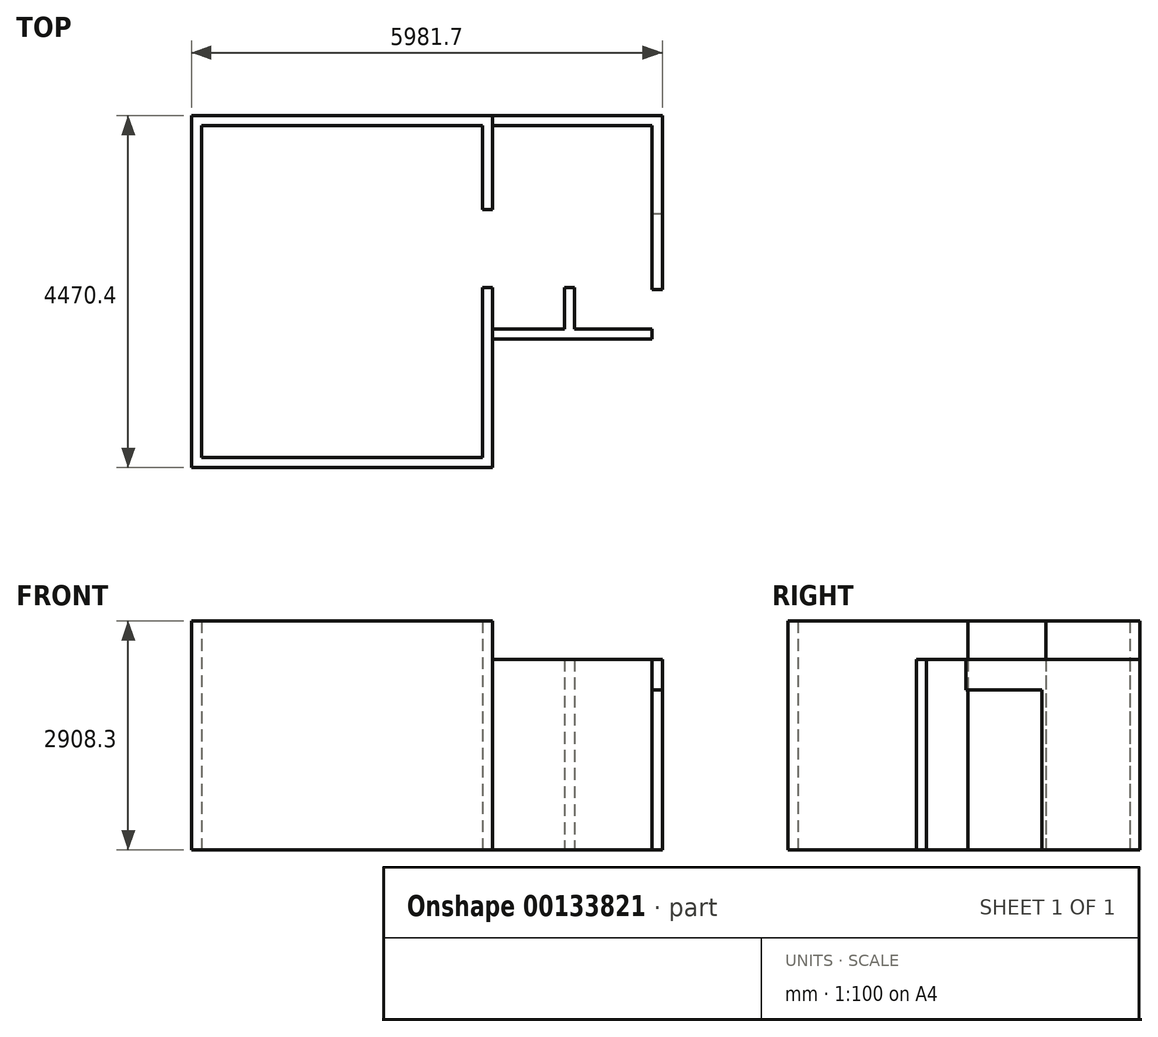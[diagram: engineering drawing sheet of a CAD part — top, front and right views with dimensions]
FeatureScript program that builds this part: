
annotation { "Feature Type Name" : "Feature", "Feature Type Description" : "" }
export const myFeature = defineFeature(function(context is Context, id is Id, definition is map)
    precondition{}
    {
        {
            var Q0;
            Q0=qCreatedBy(makeId("Top.planeOp"),FACE);
            var sketch = newSketch(context, id + "F0", { "sketchPlane" : qUnion([Q0])});
            skLineSegment(sketch, "E0.bottom", {"start": v(-3695.7, 2908.4) * mm, "end": v(-127, 2908.4) * mm});
            skLineSegment(sketch, "E0.top", {"start": v(-3695.7, -1308) * mm, "end": v(-127, -1308) * mm});
            skLineSegment(sketch, "E0.left", {"start": v(-3695.7, 2908.4) * mm, "end": v(-3695.7, -1308) * mm});
            skLineSegment(sketch, "E0.right", {"start": v(-127, 2908.4) * mm, "end": v(-127, -1308) * mm});
            skLineSegment(sketch, "E1.bottom", {"start": v(-3695.7, 2908.4) * mm, "end": v(-3479.8, 2908.4) * mm});
            skLineSegment(sketch, "E1.top", {"start": v(-3695.7, 2711.54) * mm, "end": v(-3479.8, 2711.54) * mm});
            skLineSegment(sketch, "E1.left", {"start": v(-3695.7, 2908.4) * mm, "end": v(-3695.7, 2711.54) * mm});
            skLineSegment(sketch, "E1.right", {"start": v(-3479.8, 2908.4) * mm, "end": v(-3479.8, 2711.54) * mm});
            skLineSegment(sketch, "E2.bottom", {"start": v(-127, 2908.4) * mm, "end": v(0, 2908.4) * mm});
            skLineSegment(sketch, "E2.top", {"start": v(-127, 1841.6) * mm, "end": v(0, 1841.6) * mm});
            skLineSegment(sketch, "E2.left", {"start": v(-127, 2908.4) * mm, "end": v(-127, 1841.6) * mm});
            skLineSegment(sketch, "E2.right", {"start": v(0, 2908.4) * mm, "end": v(0, 1841.6) * mm});
            skLineSegment(sketch, "E3.bottom", {"start": v(-127, -1308) * mm, "end": v(0, -1308) * mm});
            skLineSegment(sketch, "E3.top", {"start": v(-127, 851) * mm, "end": v(0, 851) * mm});
            skLineSegment(sketch, "E3.left", {"start": v(-127, -1308) * mm, "end": v(-127, 851) * mm});
            skLineSegment(sketch, "E3.right", {"start": v(0, -1308) * mm, "end": v(0, 851) * mm});
            skLineSegment(sketch, "E4.bottom", {"start": v(-3695.7, -1308) * mm, "end": v(-3479.8, -1308) * mm});
            skLineSegment(sketch, "E4.top", {"start": v(-3695.7, -1136.56) * mm, "end": v(-3479.8, -1136.56) * mm});
            skLineSegment(sketch, "E4.left", {"start": v(-3695.7, -1308) * mm, "end": v(-3695.7, -1136.56) * mm});
            skLineSegment(sketch, "E4.right", {"start": v(-3479.8, -1308) * mm, "end": v(-3479.8, -1136.56) * mm});
            skLineSegment(sketch, "E5.bottom", {"start": v(0, 851) * mm, "end": v(914.4, 851) * mm});
            skLineSegment(sketch, "E5.top", {"start": v(0, 323.94) * mm, "end": v(914.4, 323.94) * mm});
            skLineSegment(sketch, "E5.left", {"start": v(0, 851) * mm, "end": v(0, 323.94) * mm});
            skLineSegment(sketch, "E5.right", {"start": v(914.4, 851) * mm, "end": v(914.4, 323.94) * mm});
            skLineSegment(sketch, "E6.bottom", {"start": v(0, -1308) * mm, "end": v(2032, -1308) * mm});
            skLineSegment(sketch, "E6.top", {"start": v(0, 2908.4) * mm, "end": v(2032, 2908.4) * mm});
            skLineSegment(sketch, "E6.left", {"start": v(0, -1308) * mm, "end": v(0, 2908.4) * mm});
            skLineSegment(sketch, "E6.right", {"start": v(2032, -1308) * mm, "end": v(2032, 2908.4) * mm});
            skLineSegment(sketch, "E7.bottom", {"start": v(2032, 1790.8) * mm, "end": v(2184.4, 1790.8) * mm});
            skLineSegment(sketch, "E7.top", {"start": v(2032, 825.6) * mm, "end": v(2184.4, 825.6) * mm});
            skLineSegment(sketch, "E7.left", {"start": v(2032, 1790.8) * mm, "end": v(2032, 825.6) * mm});
            skLineSegment(sketch, "E7.right", {"start": v(2184.4, 1790.8) * mm, "end": v(2184.4, 825.6) * mm});
            skLineSegment(sketch, "E8.bottom", {"start": v(0, 323.94) * mm, "end": v(2032, 323.94) * mm});
            skLineSegment(sketch, "E8.left", {"start": v(0, 323.94) * mm, "end": v(0, -1308) * mm});
            skLineSegment(sketch, "E8.right", {"start": v(2032, 323.94) * mm, "end": v(2032, -1308) * mm});
            skLineSegment(sketch, "E9.bottom", {"start": v(2159, -1435) * mm, "end": v(-3822.7, -1435) * mm});
            skLineSegment(sketch, "E9.top", {"start": v(2159, 3035.4) * mm, "end": v(-3822.7, 3035.4) * mm});
            skLineSegment(sketch, "E9.left", {"start": v(2159, -1435) * mm, "end": v(2159, 3035.4) * mm});
            skLineSegment(sketch, "E9.right", {"start": v(-3822.7, -1435) * mm, "end": v(-3822.7, 3035.4) * mm});
            skLineSegment(sketch, "E10", {"start": v(0, -1308) * mm, "end": v(0, -1435) * mm});
            skLineSegment(sketch, "E11", {"start": v(0, 2908.4) * mm, "end": v(0, 3035.4) * mm});
            skLineSegment(sketch, "E12.bottom", {"start": v(914.4, 851) * mm, "end": v(1041.4, 851) * mm});
            skLineSegment(sketch, "E12.top", {"start": v(914.4, 323.94) * mm, "end": v(1041.4, 323.94) * mm});
            skLineSegment(sketch, "E12.right", {"start": v(1041.4, 851) * mm, "end": v(1041.4, 323.94) * mm});
            skLineSegment(sketch, "E13.top", {"start": v(0, 196.94) * mm, "end": v(2032, 196.94) * mm});
            skLineSegment(sketch, "E13.left", {"start": v(0, 323.94) * mm, "end": v(0, 196.94) * mm});
            skLineSegment(sketch, "E13.right", {"start": v(2032, 323.94) * mm, "end": v(2032, 196.94) * mm});
            skSolve(sketch);
        }
        {
            var Q0;
            Q0=makeQuery(id+"F0.imprint","IMPRINT",FACE,{"disambiguationData":[TD([[makeQuery(id+"F0.imprint","IMPRINT",EDGE,{"derivedFrom":sQuery(id+"F0.wireOp",EDGE,"E0.bottom")}),1.0]])]});
            var Q1;
            Q1=makeQuery(id+"F0.imprint","IMPRINT",FACE,{"disambiguationData":[TD([[makeQuery(id+"F0.imprint","IMPRINT",EDGE,{"derivedFrom":sQuery(id+"F0.wireOp",EDGE,"E3.bottom")}),1.0]])]});
            var Q2;
            {var subQ0=sQuery(id+"F0.wireOp",EDGE,"E2.bottom");Q2=makeQuery(id+"F0.imprint","IMPRINT",FACE,{"disambiguationData":[TD([[makeQuery(id+"F0.imprint","IMPRINT",EDGE,{"derivedFrom":subQ0}),-1.0]])]});}
            var Q3;
            Q3=makeQuery(id+"F0.imprint","IMPRINT",FACE,{"disambiguationData":[TD([[makeQuery(id+"F0.imprint","IMPRINT",EDGE,{"derivedFrom":sQuery(id+"F0.wireOp",EDGE,"E4.bottom")}),1.0]])]});
            var Q4;
            Q4=makeQuery(id+"F0.imprint","IMPRINT",FACE,{"disambiguationData":[TD([[makeQuery(id+"F0.imprint","IMPRINT",EDGE,{"derivedFrom":sQuery(id+"F0.wireOp",EDGE,"E1.bottom")}),-1.0]])]});
            extrude(context, id + "F1", {"entities" : qUnion([Q0, Q1, Q2, Q3, Q4]), "depth" : 2908.3 * mm});
        }
        {
            var Q0;
            {var subQ5=sQuery(id+"F0.wireOp",EDGE,"E6.top");Q0=makeQuery(id+"F0.imprint","IMPRINT",FACE,{"disambiguationData":[TD([[makeQuery(id+"F0.imprint","IMPRINT",EDGE,{"derivedFrom":subQ5}),1.0]])]});}
            var Q1;
            Q1=makeQuery(id+"F0.imprint","IMPRINT",FACE,{"disambiguationData":[TD([[makeQuery(id+"F0.imprint","IMPRINT",EDGE,{"derivedFrom":sQuery(id+"F0.wireOp",EDGE,"E12.bottom")}),-1.0]])]});
            var Q2;
            Q2=makeQuery(id+"F0.imprint","IMPRINT",FACE,{"disambiguationData":[TD([[makeQuery(id+"F0.imprint","IMPRINT",EDGE,{"derivedFrom":sQuery(id+"F0.wireOp",EDGE,"E13.top")}),1.0]])]});
            var Q3;
            Q3=makeQuery(id+"F0.imprint","IMPRINT",FACE,{"disambiguationData":[TD([[makeQuery(id+"F0.imprint","IMPRINT",EDGE,{"derivedFrom":sQuery(id+"F0.wireOp",EDGE,"E6.bottom")}),-1.0]])]});
            extrude(context, id + "F2", {"entities" : qUnion([Q0, Q1, Q2, Q3]), "operationType" : NewBodyOperationType.ADD, "depth" : 2419.35 * mm});
        }
        {
            var Q0;
            Q0=makeQuery(id+"F2.opExtrude","SWEPT_FACE",FACE,{"disambiguationData":[OSD([sQuery(id+"F0.wireOp",EDGE,"E7.bottom")])]});
            var sketch = newSketch(context, id + "F3", { "sketchPlane" : qUnion([Q0])});
            skLineSegment(sketch, "E14.bottom", {"start": v(2032, 0) * mm, "end": v(2159, 0) * mm});
            skLineSegment(sketch, "E14.top", {"start": v(2032, 2032) * mm, "end": v(2159, 2032) * mm});
            skLineSegment(sketch, "E14.left", {"start": v(2032, 0) * mm, "end": v(2032, 2032) * mm});
            skLineSegment(sketch, "E14.right", {"start": v(2159, 0) * mm, "end": v(2159, 2032) * mm});
            skSolve(sketch);
        }
        {
            var Q0;
            {var subQ0=sQuery(id+"F3.wireOp",EDGE,"E14.top");Q0=makeQuery(id+"F3.imprint","IMPRINT",FACE,{"disambiguationData":[TD([[makeQuery(id+"F3.imprint","IMPRINT",EDGE,{"derivedFrom":subQ0}),1.0]])]});}
            extrude(context, id + "F4", {"entities" : qUnion([Q0]), "operationType" : NewBodyOperationType.ADD, "depth" : 965.2 * mm});
        }
    });
